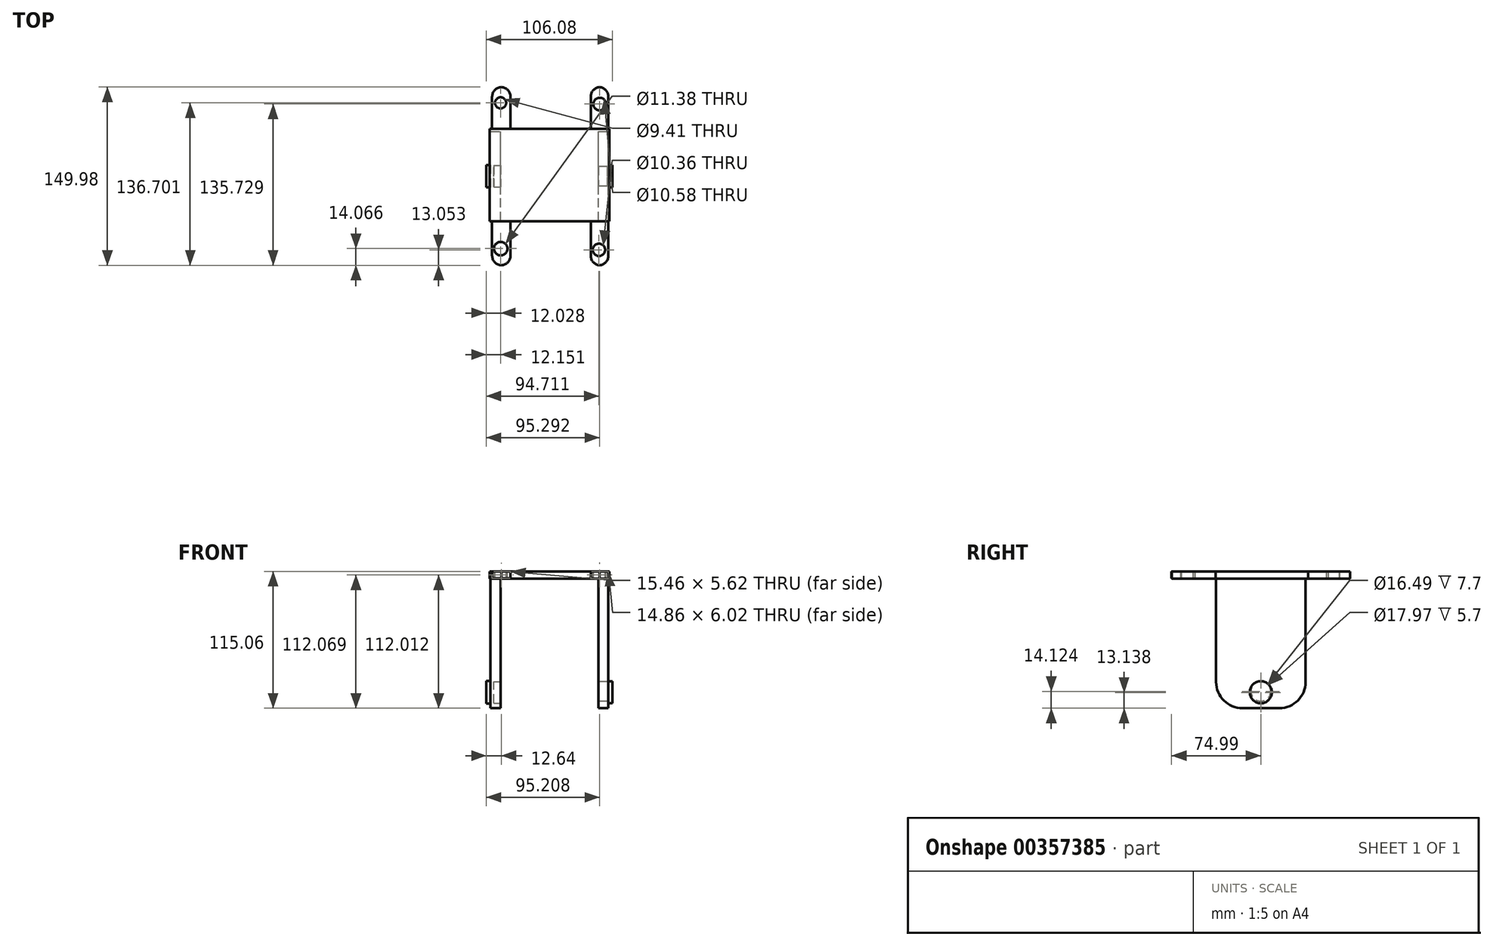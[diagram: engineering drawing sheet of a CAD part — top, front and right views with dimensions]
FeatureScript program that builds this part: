
annotation { "Feature Type Name" : "Feature", "Feature Type Description" : "" }
export const myFeature = defineFeature(function(context is Context, id is Id, definition is map)
    precondition{}
    {
        {
            var Q0;
            Q0=qCreatedBy(makeId("Right.planeOp"),FACE);
            var sketch = newSketch(context, id + "F0", { "sketchPlane" : qUnion([Q0])});
            skLineSegment(sketch, "E0.bottom", {"start": v(-38, 39.73) * mm, "end": v(39.9, 39.73) * mm});
            skLineSegment(sketch, "E0.top", {"start": v(-38, 33.5) * mm, "end": v(39.9, 33.5) * mm});
            skLineSegment(sketch, "E0.left", {"start": v(-38, 39.73) * mm, "end": v(-38, 33.5) * mm});
            skLineSegment(sketch, "E0.right", {"start": v(39.9, 39.73) * mm, "end": v(39.9, 33.5) * mm});
            skSolve(sketch);
        }
        {
            var Q0;
            Q0=makeQuery(id+"F0.imprint","IMPRINT",FACE,{"disambiguationData":[TD([[makeQuery(id+"F0.imprint","IMPRINT",EDGE,{"derivedFrom":sQuery(id+"F0.wireOp",EDGE,"E0.bottom")}),-1.0]])]});
            extrude(context, id + "F1", {"entities" : qUnion([Q0]), "endBound" : BoundingType.SYMMETRIC, "depth" : 100.58 * mm});
        }
        {
            var Q0;
            Q0=qCreatedBy(makeId("Front.planeOp"),FACE);
            var sketch = newSketch(context, id + "F2", { "sketchPlane" : qUnion([Q0])});
            skLineSegment(sketch, "E1.bottom", {"start": v(47.04, 34.02) * mm, "end": v(41.07, 34.02) * mm});
            skLineSegment(sketch, "E1.top", {"start": v(47.04, -75.33) * mm, "end": v(41.07, -75.33) * mm});
            skLineSegment(sketch, "E1.left", {"start": v(47.04, 34.02) * mm, "end": v(47.04, -75.33) * mm});
            skLineSegment(sketch, "E1.right", {"start": v(41.07, 34.02) * mm, "end": v(41.07, -75.33) * mm});
            skLineSegment(sketch, "E2.bottom", {"start": v(-41.07, 34.5) * mm, "end": v(-47.27, 34.5) * mm});
            skLineSegment(sketch, "E2.top", {"start": v(-41.07, -75.33) * mm, "end": v(-47.27, -75.33) * mm});
            skLineSegment(sketch, "E2.left", {"start": v(-41.07, 34.5) * mm, "end": v(-41.07, -75.33) * mm});
            skLineSegment(sketch, "E2.right", {"start": v(-47.27, 34.5) * mm, "end": v(-47.27, -75.33) * mm});
            skSolve(sketch);
        }
        {
            var Q0;
            Q0 = qSketchRegion(id + "F2", true);
            extrude(context, id + "F3", {"entities" : qUnion([Q0]), "operationType" : NewBodyOperationType.ADD, "endBound" : BoundingType.SYMMETRIC, "depth" : 75.18 * mm});
        }
        {
            var Q0;
            Q0=makeQuery(id+"F3.opExtrude","CAP_EDGE",EDGE,{"disambiguationData":[OSD([sQuery(id+"F2.wireOp",EDGE,"E1.top")])],"isStart":true});
            var Q1;
            Q1=makeQuery(id+"F3.opExtrude","CAP_EDGE",EDGE,{"disambiguationData":[OSD([sQuery(id+"F2.wireOp",EDGE,"E1.top")])],"isStart":false});
            var Q2;
            Q2=makeQuery(id+"F3.opExtrude","CAP_EDGE",EDGE,{"disambiguationData":[OSD([sQuery(id+"F2.wireOp",EDGE,"E2.top")])],"isStart":false});
            var Q3;
            Q3=makeQuery(id+"F3.opExtrude","CAP_EDGE",EDGE,{"disambiguationData":[OSD([sQuery(id+"F2.wireOp",EDGE,"E2.top")])],"isStart":true});
            fillet(context, id + "F4", {"entities" : qUnion([Q0, Q1, Q2, Q3]), "radius" : 22.08 * mm, "tangentPropagation" : true, "allowEdgeOverflow" : false});
        }
        {
            var Q0;
            Q0=makeQuery(id+"F3.opExtrude","SWEPT_FACE",FACE,{"disambiguationData":[OSD([sQuery(id+"F2.wireOp",EDGE,"E1.left")])]});
            var Q1;
            Q1=makeQuery(id+"F3.opExtrude","SWEPT_FACE",FACE,{"disambiguationData":[OSD([sQuery(id+"F2.wireOp",EDGE,"E2.right")])]});
            extrude(context, id + "F5", {"entities" : qUnion([Q0, Q1]), "operationType" : NewBodyOperationType.ADD, "endBound" : BoundingType.SYMMETRIC, "depth" : 4.57 * mm});
        }
        {
            var Q0;
            Q0=makeQuery(id+"F5.opExtrude","CAP_FACE",FACE,{"disambiguationData":[OSD([sQuery(id+"F2.wireOp",EDGE,"E1.left")])],"isStart":false});
            var sketch = newSketch(context, id + "F6", { "sketchPlane" : qUnion([Q0])});
            skCircle(sketch, "E3", {"center": v(0, -61.93) * mm, "radius": 9.31 * mm});
            skCircle(sketch, "E4", {"center": v(0, -61.93) * mm, "radius": 9.3 * mm});
            skCircle(sketch, "E5", {"center": v(0, -61.93) * mm, "radius": 9.27 * mm});
            skCircle(sketch, "E6", {"center": v(0, -61.93) * mm, "radius": 9.26 * mm});
            skSolve(sketch);
        }
        {
            var Q0;
            Q0=makeQuery(id+"F5.opExtrude","CAP_FACE",FACE,{"disambiguationData":[OSD([sQuery(id+"F2.wireOp",EDGE,"E2.right")])],"isStart":true});
            var sketch = newSketch(context, id + "F7", { "sketchPlane" : qUnion([Q0])});
            skCircle(sketch, "E7", {"center": v(0, -61.96) * mm, "radius": 9.5 * mm});
            skSolve(sketch);
        }
        {
            var Q0;
            Q0=makeQuery(id+"F7.imprint","IMPRINT",FACE,{"disambiguationData":[TD([[makeQuery(id+"F7.imprint","IMPRINT",EDGE,{"derivedFrom":sQuery(id+"F7.wireOp",EDGE,"E7")}),1.0]])]});
            extrude(context, id + "F8", {"entities" : qUnion([Q0]), "operationType" : NewBodyOperationType.ADD, "depth" : 3.6 * mm});
        }
        {
            var Q0;
            Q0=makeQuery(id+"F6.imprint","IMPRINT",FACE,{"disambiguationData":[TD([[makeQuery(id+"F6.imprint","IMPRINT",EDGE,{"derivedFrom":sQuery(id+"F6.wireOp",EDGE,"E6")}),1.0]])]});
            var Q1;
            Q1=sQuery(id+"F6.wireOp",EDGE,"E4");
            extrude(context, id + "F9", {"entities" : qUnion([Q0]), "operationType" : NewBodyOperationType.ADD, "surfaceEntities" : qUnion([Q1]), "depth" : 3.6 * mm});
        }
        {
            var Q0;
            Q0=makeQuery(id+"F3.opExtrude","SWEPT_FACE",FACE,{"disambiguationData":[OSD([sQuery(id+"F2.wireOp",EDGE,"E1.right")])]});
            var sketch = newSketch(context, id + "F10", { "sketchPlane" : qUnion([Q0])});
            skCircle(sketch, "E8", {"center": v(0, -61.2) * mm, "radius": 8.25 * mm});
            skSolve(sketch);
        }
        {
            var Q0;
            Q0=makeQuery(id+"F3.opExtrude","SWEPT_FACE",FACE,{"disambiguationData":[OSD([sQuery(id+"F2.wireOp",EDGE,"E2.left")])]});
            var sketch = newSketch(context, id + "F11", { "sketchPlane" : qUnion([Q0])});
            skCircle(sketch, "E9", {"center": v(0, -62.2) * mm, "radius": 8.99 * mm});
            skSolve(sketch);
        }
        {
            var Q0;
            Q0=makeQuery(id+"F10.imprint","IMPRINT",FACE,{"disambiguationData":[TD([[makeQuery(id+"F10.imprint","IMPRINT",EDGE,{"derivedFrom":sQuery(id+"F10.wireOp",EDGE,"E8")}),1.0]])]});
            var Q1;
            Q1=sQuery(id+"F10.wireOp",EDGE,"E8");
            extrude(context, id + "F12", {"entities" : qUnion([Q0]), "operationType" : NewBodyOperationType.REMOVE, "surfaceEntities" : qUnion([Q1]), "oppositeDirection" : true, "depth" : 7.7 * mm});
        }
        {
            var Q0;
            Q0=makeQuery(id+"F11.imprint","IMPRINT",FACE,{"disambiguationData":[TD([[makeQuery(id+"F11.imprint","IMPRINT",EDGE,{"derivedFrom":sQuery(id+"F11.wireOp",EDGE,"E9")}),1.0]])]});
            extrude(context, id + "F13", {"entities" : qUnion([Q0]), "operationType" : NewBodyOperationType.REMOVE, "oppositeDirection" : true, "depth" : 5.7 * mm});
        }
        {
            var Q0;
            Q0=qCreatedBy(makeId("Front.planeOp"),FACE);
            var sketch = newSketch(context, id + "F14", { "sketchPlane" : qUnion([Q0])});
            skLineSegment(sketch, "E10.bottom", {"start": v(49.48, 39.7) * mm, "end": v(34.62, 39.7) * mm});
            skLineSegment(sketch, "E10.top", {"start": v(49.48, 33.67) * mm, "end": v(34.62, 33.67) * mm});
            skLineSegment(sketch, "E10.left", {"start": v(49.48, 39.7) * mm, "end": v(49.48, 33.67) * mm});
            skLineSegment(sketch, "E10.right", {"start": v(34.62, 39.7) * mm, "end": v(34.62, 33.67) * mm});
            skLineSegment(sketch, "E11.bottom", {"start": v(-48.25, 39.55) * mm, "end": v(-32.79, 39.55) * mm});
            skLineSegment(sketch, "E11.top", {"start": v(-48.25, 33.93) * mm, "end": v(-32.79, 33.93) * mm});
            skLineSegment(sketch, "E11.left", {"start": v(-48.25, 39.55) * mm, "end": v(-48.25, 33.93) * mm});
            skLineSegment(sketch, "E11.right", {"start": v(-32.79, 39.55) * mm, "end": v(-32.79, 33.93) * mm});
            skSolve(sketch);
        }
        {
            var Q0;
            Q0 = qSketchRegion(id + "F14", true);
            extrude(context, id + "F15", {"entities" : qUnion([Q0]), "operationType" : NewBodyOperationType.ADD, "endBound" : BoundingType.SYMMETRIC, "depth" : 150 * mm});
        }
        {
            var Q0;
            Q0=makeQuery(id+"F15.opExtrude","CAP_EDGE",EDGE,{"disambiguationData":[OSD([sQuery(id+"F14.wireOp",EDGE,"E11.right")])],"isStart":true});
            var Q1;
            Q1=makeQuery(id+"F15.opExtrude","CAP_EDGE",EDGE,{"disambiguationData":[OSD([sQuery(id+"F14.wireOp",EDGE,"E11.left")])],"isStart":true});
            var Q2;
            Q2=makeQuery(id+"F15.opExtrude","CAP_EDGE",EDGE,{"disambiguationData":[OSD([sQuery(id+"F14.wireOp",EDGE,"E10.left")])],"isStart":true});
            var Q3;
            Q3=makeQuery(id+"F15.opExtrude","CAP_EDGE",EDGE,{"disambiguationData":[OSD([sQuery(id+"F14.wireOp",EDGE,"E10.right")])],"isStart":true});
            var Q4;
            Q4=makeQuery(id+"F15.opExtrude","CAP_EDGE",EDGE,{"disambiguationData":[OSD([sQuery(id+"F14.wireOp",EDGE,"E10.left")])],"isStart":false});
            var Q5;
            Q5=makeQuery(id+"F15.opExtrude","CAP_EDGE",EDGE,{"disambiguationData":[OSD([sQuery(id+"F14.wireOp",EDGE,"E10.right")])],"isStart":false});
            var Q6;
            Q6=makeQuery(id+"F15.opExtrude","CAP_EDGE",EDGE,{"disambiguationData":[OSD([sQuery(id+"F14.wireOp",EDGE,"E11.left")])],"isStart":false});
            var Q7;
            Q7=makeQuery(id+"F15.opExtrude","CAP_EDGE",EDGE,{"disambiguationData":[OSD([sQuery(id+"F14.wireOp",EDGE,"E11.right")])],"isStart":false});
            fillet(context, id + "F16", {"entities" : qUnion([Q0, Q1, Q2, Q3, Q4, Q5, Q6, Q7]), "radius" : 8.2 * mm, "tangentPropagation" : true, "allowEdgeOverflow" : false});
        }
        {
            var Q0;
            {var subQ2=sQuery(id+"F14.wireOp",EDGE,"E10.bottom");Q0=makeQuery(id+"F15.boolean.opBoolean","SPLIT",FACE,{"disambiguationData":[TD([makeQuery(id+"F1.opExtrude","SWEPT_FACE",FACE,{"disambiguationData":[OSD([sQuery(id+"F0.wireOp",EDGE,"E0.right")])]})])],"derivedFrom":makeQuery(id+"F15.opExtrude","SWEPT_FACE",FACE,{"disambiguationData":[OSD([subQ2])]})});}
            var sketch = newSketch(context, id + "F17", { "sketchPlane" : qUnion([Q0])});
            skCircle(sketch, "E12", {"center": v(-41.13, 61.71) * mm, "radius": 4.7 * mm});
            skCircle(sketch, "E13", {"center": v(42.13, 60.74) * mm, "radius": 5.29 * mm});
            skCircle(sketch, "E14", {"center": v(-41, -60.92) * mm, "radius": 5.7 * mm});
            skCircle(sketch, "E15", {"center": v(41.55, -61.94) * mm, "radius": 5.18 * mm});
            skSolve(sketch);
        }
        {
            var Q0;
            Q0=makeQuery(id+"F17.imprint","IMPRINT",FACE,{"disambiguationData":[TD([[makeQuery(id+"F17.imprint","IMPRINT",EDGE,{"derivedFrom":sQuery(id+"F17.wireOp",EDGE,"E12")}),1.0]])]});
            var Q1;
            Q1 = qSketchRegion(id + "F17", true);
            extrude(context, id + "F18", {"entities" : qUnion([Q0, Q1]), "operationType" : NewBodyOperationType.REMOVE, "oppositeDirection" : true, "depth" : 25 * mm});
        }
    });
